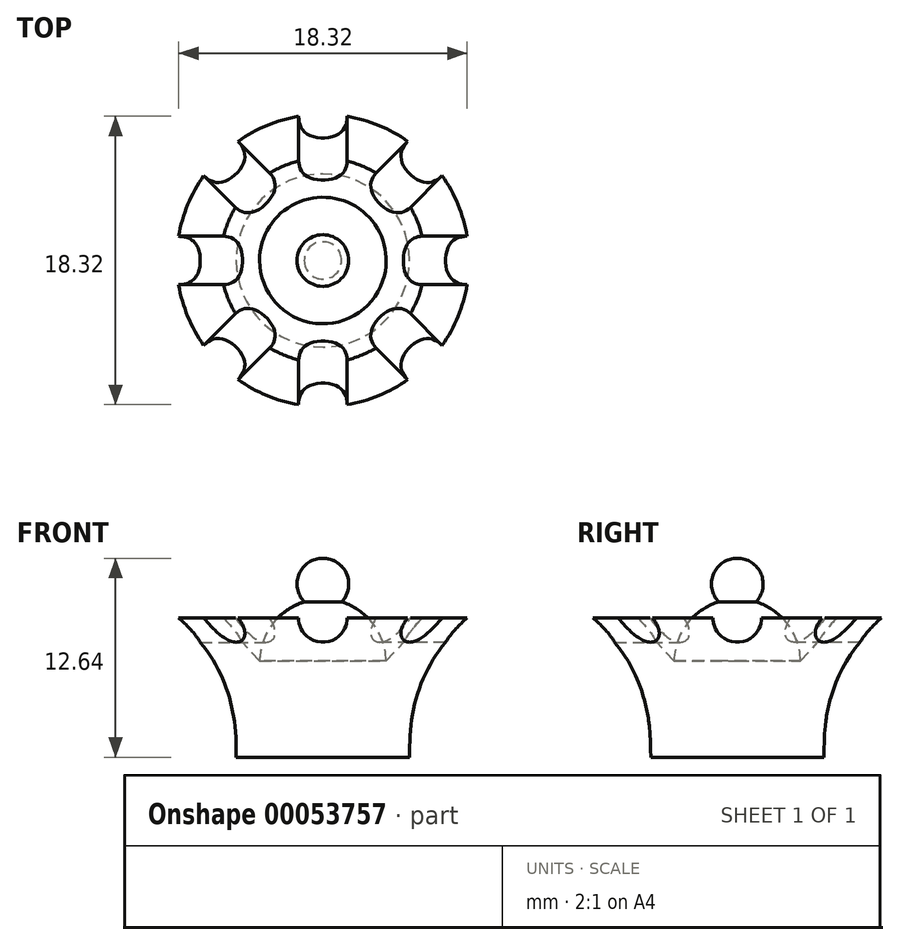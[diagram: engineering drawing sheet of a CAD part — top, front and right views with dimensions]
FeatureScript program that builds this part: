
annotation { "Feature Type Name" : "Feature", "Feature Type Description" : "" }
export const myFeature = defineFeature(function(context is Context, id is Id, definition is map)
    precondition{}
    {
        {
            var Q0;
            Q0=qCreatedBy(makeId("Front.planeOp"),FACE);
            var sketch = newSketch(context, id + "F0", { "sketchPlane" : qUnion([Q0])});
            skLineSegment(sketch, "E0", {"start": v(0, 0) * mm, "end": v(-5.5, 0) * mm});
            skFitSpline(sketch, "E1", {"points": [v(-5.5, 0) * mm, v(-5.84, 3.4) * mm, v(-6.93, 6.09) * mm, v(-9.29, 8.84) * mm], "startDerivative": vector(0, 13.29) * mm, "endDerivative": vector(-8.63, 7.62) * mm});
            skLineSegment(sketch, "E2", {"start": v(-9.29, 8.84) * mm, "end": v(-6.5, 8.84) * mm});
            skLineSegment(sketch, "E3", {"start": v(-6.5, 8.84) * mm, "end": v(-4.02, 6.1) * mm});
            skArc(sketch, "E4", {"start": v(0, 10.05) * mm, "mid": v(-2.82, 8.9) * mm, "end": v(-4.02, 6.1) * mm});
            skLineSegment(sketch, "E5", {"start": v(0, 0) * mm, "end": v(0, 20.1) * mm});
            skArc(sketch, "E6", {"start": v(0, 12.64) * mm, "mid": v(-1.64, 11) * mm, "end": v(0, 9.36) * mm});
            skSolve(sketch);
        }
        {
            var Q0;
            Q0 = qSketchRegion(id + "F0", true);
            var Q1;
            Q1=sQuery(id+"F0.wireOp",EDGE,"E5");
            revolve(context, id + "F1", {"entities" : qUnion([Q0]), "axis" : qUnion([Q1]), "revolveType" : RevolveType.FULL});
        }
        {
            var Q0;
            Q0=makeQuery(id+"F1.opRevolve","SWEPT_FACE",FACE,{"disambiguationData":[OSD([sQuery(id+"F0.wireOp",EDGE,"E2")])]});
            var sketch = newSketch(context, id + "F2", { "sketchPlane" : qUnion([Q0])});
            skCircle(sketch, "E7.0", {"center": v(0, 0) * mm, "radius": 9.29 * mm, "construction": true});
            skCircle(sketch, "E8.0", {"center": v(0, 0) * mm, "radius": 4.02 * mm, "construction": true});
            skLineSegment(sketch, "E9", {"start": v(0, 0) * mm, "end": v(0, 33.23) * mm});
            skLineSegment(sketch, "E10", {"start": v(0, 4.02) * mm, "end": v(-1.54, 4.02) * mm});
            skLineSegment(sketch, "E11", {"start": v(0, 9.29) * mm, "end": v(-1.54, 9.29) * mm});
            skLineSegment(sketch, "E12", {"start": v(-1.54, 9.29) * mm, "end": v(-1.54, 4.02) * mm});
            skSolve(sketch);
        }
        {
            var Q0;
            Q0 = qSketchRegion(id + "F2", true);
            var Q1;
            Q1 = qConstructionFilter(qBodyType(qCreatedBy(id + "F2" ,EDGE), BodyType.WIRE), ConstructionObject.NO);
            var Q2;
            Q2=sQuery(id+"F2.wireOp",EDGE,"E9");
            revolve(context, id + "F3", {"entities" : qUnion([Q0]), "surfaceEntities" : qUnion([Q1]), "axis" : qUnion([Q2]), "revolveType" : RevolveType.FULL});
        }
        {
            var Q0;
            Q0=makeQuery(id+"F3.opRevolve","SWEPT_BODY",BODY,{"disambiguationData":[OSD([sQuery(id+"F2.wireOp",EDGE,"E9"),sQuery(id+"F2.wireOp",EDGE,"E10"),sQuery(id+"F2.wireOp",EDGE,"E11"),sQuery(id+"F2.wireOp",EDGE,"E12")])]});
            var Q1;
            Q1=sQuery(id+"F0.wireOp",EDGE,"E5");
            circularPattern(context, id + "F4", {"operationType" : NewBodyOperationType.REMOVE, "entities" : qUnion([Q0]), "axis" : qUnion([Q1]), "angle" : 45 * degree, "instanceCount" : 8});
        }
    });
